# Revit family: 64412210
name_source: partatom
category: Plumbing Fixtures
revit_build: Autodesk Revit 2016 (Build: 20150714_1515(x64)
units: mm (PartAtom-declared; Revit-internal decimal feet)

## family parameters
Always vertical = Yes
Cut with Voids When Loaded = No
OmniClass Number = 23.45.55.00
OmniClass Title = Sanitary Faucets, Wastes
Part Type = Normal
Room Calculation Point = No
Round Connector Dimension = Use Diameter
Shared = No
Work Plane-Based = No

## types (1)
- 64412210 Washbasin faucet, 6 V
    2D/3D/BIM Files URL = http://static.hansa.com
    Advanced Features = Vandal-proof construction; Convertible for cold and premixed-water; Without draw-rod opening
    Aerator = Pressure controlled aerator; CASCADE
    Approval ACS = 15 ACC LY 337
    Approval CSTB = 322-M1-17/1
    Approval WRAS = 1301013
    AssetType = Fixed
    BIMObjectName = 64412210
    Backflow Prevention EN1717 = EB
    Battery = Lithium 2CR5 6 V
    BodyMaterial = Brass
    Brand = Hansa
    Catalog Drawing URL = http://static.hansa.com
    Category = Bathroom, public, health care
    Class = Battery-operated, touchless
    CloseOffRating = 0
    Color = Chrome
    Connection Size = G3/8
    ConvergoRefNr = 0087-1710-0022-DE
    Customs Code = 84818011
    DN Size = DN15
    Dimension Drawing URL = http://static.hansa.com
    DurationUnit = Year
    EAN Number = 4015474273337
    EMC Directive = 89/336/EEC
    EN Standard = EN 15091
    ETA-Danmark = VA 1.42/18729
    Electronic Parts = Autofocus sensor; Solenoid valve; Low battery indication
    Extensions = No pop-up waste included
    FDV Document URL = http://www.hansa.com
    FaucetMainMaterial = Brass
    Features = Battery-operated
    Finish = Polished
    Flow Drawing URL = http://static.hansa.com
    Flow Rate At 300kPa With Flow Controller = 0.1 L/s
    FlowCoefficient = 0
    Group = Washbasin Faucets
    Health Sales Arguments = Touch-free operation. Maximum comfort, maximum hygiene.
    IfcExportAs = IfcValveType
    IfcExportType = FAUCET
    InletConnectionSize = 10 mm  [stored 0.0328084 ft]
    Installation Type = Deck mounted
    Installation and Maintenance = http://static.hansa.com
    Intelligent After Flow Period = 2 s ± 1 s
    Long Marketing = Adjustable mixed water temperature (fixed setting possible). Convertible for cold- and premixed-water. Fitting can be deactived for cleaning, with the added cover. Push-pop-up waste 59913988 can be ordered separately.
    ManufacterURL = http://www.hansa.com
    Manufacturer = Hansa
    ManufacturerName = Hansa
    Market = AUT;BEL;CZE;DEU;ESP;FRA;INT;ITA;NLD;SVK
    Material = Brass
    Max Flow Period = 120.0 s
    Max. Hot Water Supply = 70 °C
    Mechanical Parts = Non-return valve(s); Litter filter(s)
    Model = 64412210 Washbasin faucet, 6 V
    ModelReference = 64412210
    Mounting Holes = 1 mounting hole
    NBSDescription = Water supply fittings for baths
    NBSReference = 45-35-70/315
    Name = 64412210 Washbasin faucet, 6 V
    Name_en = 64412210 Washbasin faucet, 6 V
    Noise Class = I (ISO 3822)
    NominalDepth = 140 mm  [stored 0.459318 ft]
    NominalHeight = 121 mm
    NominalWidth = 65 mm  [stored 0.213255 ft]
    Operating Voltage = 6 V
    Package Weight = 1.693 kg
    Package external Dimensions = 290 x 210 x 90
    Pipes = Flexible inlet pipe(s)
    Pressure Loss With Flow 01ls = 200000.0 Pa
    Product Code = 64412210
    Product Datasheet = http://www.hansa.com
    Product Family = Hansaelectra
    Product Image URL = http://static.hansa.com
    Product URL = http://static.hansa.com
    Projection = 96 mm  [stored 0.314961 ft]
    Protection Class = IP 55
    Recognition Range = Optimally preset
    Revision = 2
    STF Certificate = STF VTT-RTH-00031-11
    Shape = Sculptured
    Sintef Certificate = Sintef Nr. 1534
    Size = 65x140x120.5 mm
    Spare Parts = http://static.hansa.com
    Spout Type = Fixed spout
    Temperature = Temperature fixable; Temperature regulator
    URL ACS = http://static.hansa.com
    URL CSTB = http://static.hansa.com
    URL ETA-Danmark = http://static.hansa.com
    URL SINTEF = http://static.hansa.com
    URL STF = http://static.hansa.com
    URL WRAS = http://static.hansa.com
    Uniclass2 = Pr_40_30_96_78
    Uniclass2015Description = Shower manual water supply sets
    Uniclass2015Reference = Pr_40_20_87_78
    Usage Group = Offices, personnel sanitary facilities; Toilets for the Disabled; Pharmacies, Opticians, Dentists; Health centers & Child welfare clinics; Hospitals;Food stores;Gas stations; Schools; Households
    Version = 2
    VersionDate = 01/01/2019
    WarrantyDescription = http://warranty.hansa.com
    WarrantyDurationUnit = Year
    WorkingPressure = 100 - 1000 kPa

note: [stored X ft] marks values corroborated as IEEE doubles in the binary element streams (Revit-internal decimal feet)

## geometry (parser evidence)
native form markers: Sweep x4
no freeform markers — native parametric forms only
